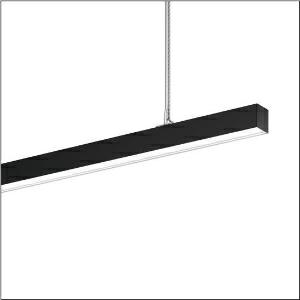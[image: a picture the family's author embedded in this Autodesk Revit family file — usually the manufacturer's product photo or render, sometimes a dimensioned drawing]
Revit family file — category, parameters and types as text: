
# Revit family: silica_r__21_51mx33db39bb_fd0d
name_source: partatom
category: Lighting Fixtures
units: mm (PartAtom-declared; Revit-internal decimal feet)

## family parameters
Cut with Voids When Loaded = No
Host = Face
Light Source = No
Part Type = Normal
Room Calculation Point = No
Round Connector Dimension = Use Diameter
Shared = No

## types (1)
- --- (1 x LED, 7390 lm, 51.6 W, 3000K)
    Apparent Load = 52 VA
    CIE Flux Codes = 78 96 99 55 100
    Color Rendering = 80
    Color Temperature = 3000K
    Default Elevation = 1800 mm
    Description = Silica® 21, office luminaire, primary optical cover: prismatic diffuser, of PMMA, CAT 2 (L<= 3000cd/m²), light emission: direct/indirect distribution, primary light characteristic: symmetric, installation type: suspended mounting, LED, rated luminous flux: 7.390lm, luminous efficacy: 143lm/W, light colour: 830, colour temperature: 3000K, with terminal, 3+2-pole, max. 2.5mm², mains connection: 220..240V, AC, 50/60Hz, rated input power: 51.6W, luminaire housing, of aluminium, jet black (RAL 9005), length: 1.504mm, width: 53mm, height: 53mm, protection rating (complete): IP20, insulation class (complete): insulation class I (protective earthing), certification: CE, permissible operating ambient temperature: 0..+35°C, standard: EN 50419, packaging unit: 1 piece
    Height = 53 mm
    Lamp = 1 x LED
    Lamp Light Flux = 7390 lm
    Lamp Power = 51.6 W
    Lamp count = 1
    Length = 1504 mm
    Luminous efficacy = 143 lm/W
    Manufacturer = Siteco
    ModVariant = No
    Model = 51MX33DB39BB
    Mounting Place = Ceiling
    Mounting Type = Pendant
    Number of Poles = 1
    OnlyDefault = Yes
    Power Factor = 1
    Product Name = Silica® 21
    Product group = office luminaire | ceiling pendant
    ProductGroupID = 902
    Protection Class = Protection class I
    Protection Degree = IP 20
    RLX_Detail_Level = 1
    RLX_Emergency_Light_Flux = 0 lm
    RLX_Emergency_Type = 0
    RLX_Emergency_Type_DB = No
    RlxData = <blob elided: 26177 chars, md5=546f0d6a>
    Socket = socket
    Standby Power = 0 W
    System Light Flux = 7390 lm
    System Power = 52 W
    Type Comments = factory setting: luminous flux: 100 % | dim-lin: 254 | 345 mA
    Type Image = l_1297744.jpg
    URL = http://relux.com
    VarID = @adj_048737
    Voltage = 0 V
    Weight = 0.00 kg
    Width = 53 mm

## geometry (parser evidence)
native form markers: Blend x4, Sweep x14
no freeform markers — native parametric forms only
